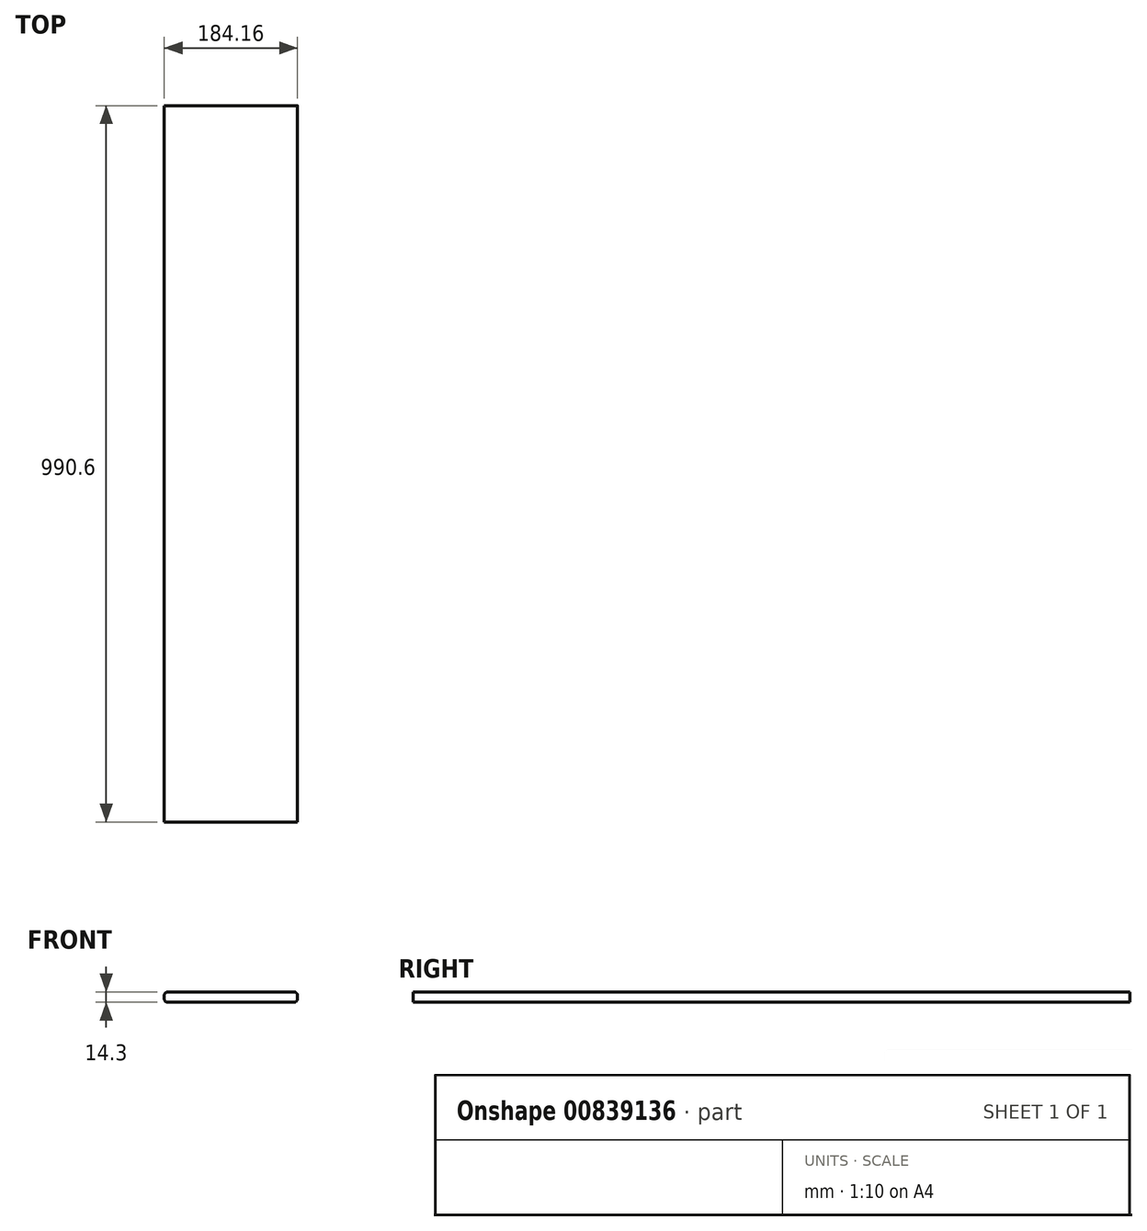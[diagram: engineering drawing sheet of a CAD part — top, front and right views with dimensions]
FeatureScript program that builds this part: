
annotation { "Feature Type Name" : "Feature", "Feature Type Description" : "" }
export const myFeature = defineFeature(function(context is Context, id is Id, definition is map)
    precondition{}
    {
        {
            var Q0;
            Q0=qCreatedBy(makeId("Front.planeOp"),FACE);
            var sketch = newSketch(context, id + "F0", { "sketchPlane" : qUnion([Q0])});
            skLineSegment(sketch, "E0.bottom", {"start": v(-87.25, 7.15) * mm, "end": v(87.25, 7.15) * mm});
            skLineSegment(sketch, "E0.top", {"start": v(-87.25, -7.15) * mm, "end": v(87.25, -7.15) * mm});
            skLineSegment(sketch, "E0.left", {"start": v(-92.08, 2.32) * mm, "end": v(-92.08, -2.32) * mm});
            skLineSegment(sketch, "E0.right", {"start": v(92.08, 2.32) * mm, "end": v(92.08, -2.32) * mm});
            skPoint(sketch, "E0.middle", {"position": v(0, 0) * mm});
            skPoint(sketch, "E1.visualSharp", {"position": v(-92.08, 7.15) * mm});
            skArc(sketch, "E1.filletArc", {"start": v(-87.25, 7.15) * mm, "mid": v(-90.66, 5.74) * mm, "end": v(-92.07, 2.32) * mm});
            skPoint(sketch, "E2.visualSharp", {"position": v(92.08, 7.15) * mm});
            skArc(sketch, "E2.filletArc", {"start": v(92.08, 2.32) * mm, "mid": v(90.66, 5.74) * mm, "end": v(87.25, 7.15) * mm});
            skPoint(sketch, "E3.visualSharp", {"position": v(92.08, -7.15) * mm});
            skArc(sketch, "E3.filletArc", {"start": v(87.25, -7.15) * mm, "mid": v(90.66, -5.74) * mm, "end": v(92.08, -2.32) * mm});
            skPoint(sketch, "E4.visualSharp", {"position": v(-92.08, -7.15) * mm});
            skArc(sketch, "E4.filletArc", {"start": v(-92.08, -2.32) * mm, "mid": v(-90.66, -5.74) * mm, "end": v(-87.25, -7.15) * mm});
            skSolve(sketch);
        }
        {
            var Q0;
            Q0=makeQuery(id+"F0.imprint","IMPRINT",FACE,{"disambiguationData":[TD([[makeQuery(id+"F0.imprint","IMPRINT",EDGE,{"derivedFrom":sQuery(id+"F0.wireOp",EDGE,"E0.bottom")}),-1.0]])]});
            extrude(context, id + "F1", {"entities" : qUnion([Q0]), "endBound" : BoundingType.SYMMETRIC, "depth" : 990.6 * mm, "offsetDistance" : 25.4 * mm});
        }
    });
